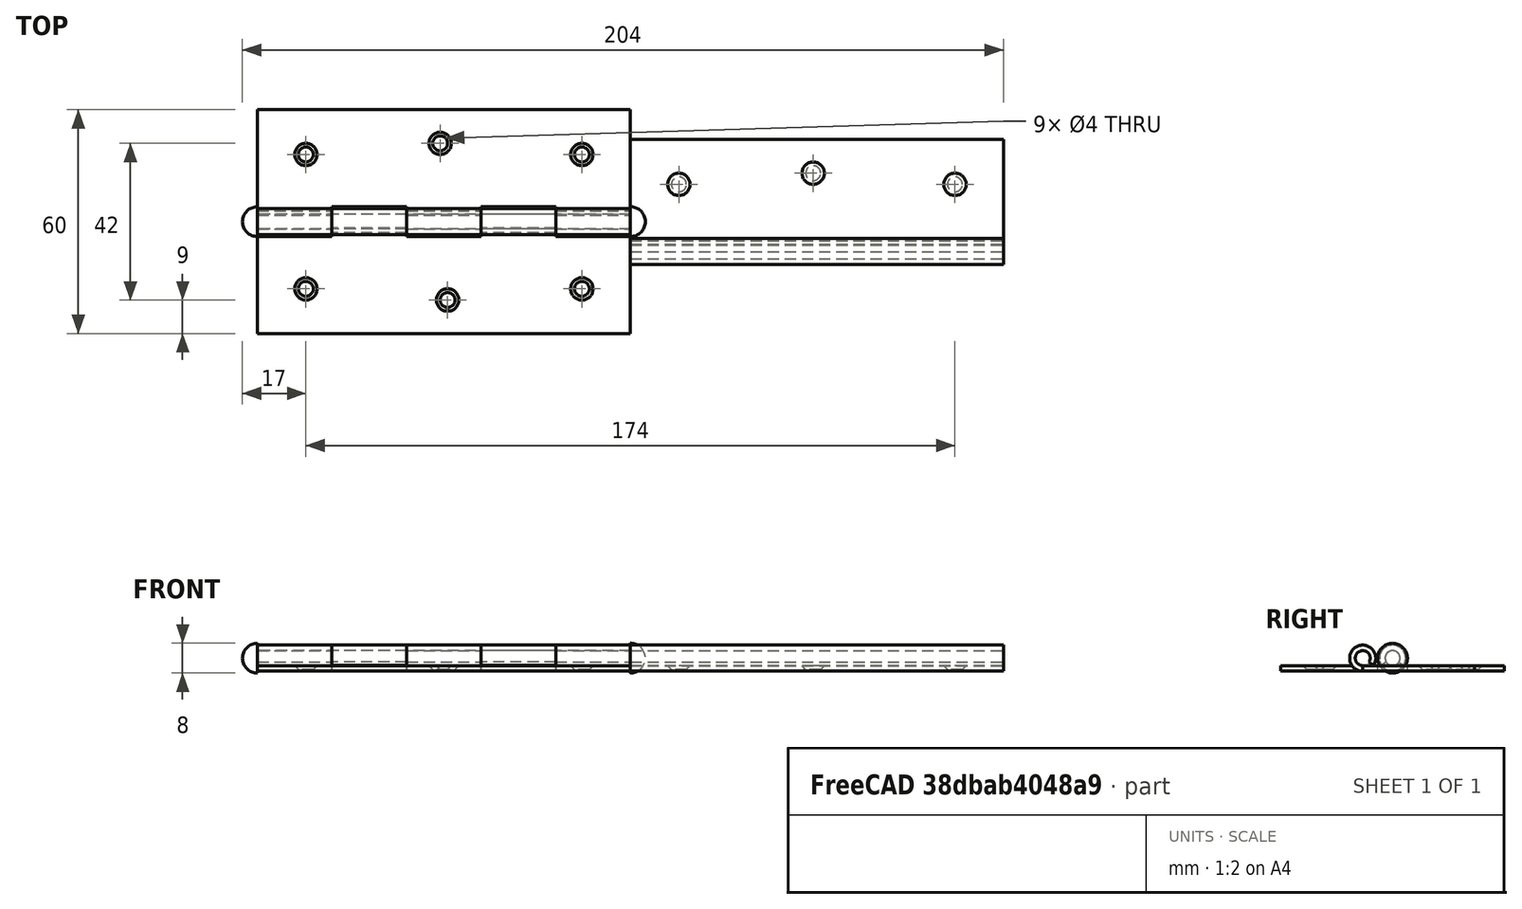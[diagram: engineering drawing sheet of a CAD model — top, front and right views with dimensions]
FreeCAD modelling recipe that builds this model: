
FCSTD DOCUMENT  (FreeCAD 0.18R13524 (Git))
Label: ABRAÇADEIRA
License: All rights reserved
LicenseURL: http://en.wikipedia.org/wiki/All_rights_reserved
objects: Part::Cut×11, Part::Box×7, Part::Cylinder×7, App::FeaturePython×3, Part::FeaturePython×2, Part::Chamfer×2, Part::Sphere×2, Part::MultiFuse×2, Part::Feature×1
note: 34 computed .brp shape members not serialized (recipe doc carries the construction recipe); baked Part::Feature solids carry a one-line shape summary decoded from their .brp

FEATURE [Part::Box] Box  label="Cube"
  AttacherType = Attacher::AttachEngine3D
  Height = 1.5
  Length = 100
  Width = 30
FEATURE [Part::FeaturePython] Bend  # WARN: FeaturePython — macro-defined, semantics opaque (R4)
  angle = 303
  baseObject = -> Box [Face3]
  gap1 = 0
  gap2 = 0
  invert = false
  length = 0
  miterangle1 = 0
  miterangle2 = 0
  radius = 2
  reliefd = 1
  reliefw = 0.5
FEATURE [Part::Cylinder] Cylinder
  Angle = 360
  AttacherType = Attacher::AttachEngine3D
  Height = 10
  Placement = pos=(13,18,0) rot=(0,0,1;0rad)
  Radius = 2
FEATURE [Part::Cylinder] Cylinder001
  Angle = 360
  AttacherType = Attacher::AttachEngine3D
  Height = 10
  Placement = pos=(49,21,0) rot=(0,0,1;0rad)
  Radius = 2
FEATURE [Part::Cylinder] Cylinder002
  Angle = 360
  AttacherType = Attacher::AttachEngine3D
  Height = 10
  Placement = pos=(87,18,0) rot=(0,0,1;0rad)
  Radius = 2
FEATURE [Part::Cut] Cut
  Base = -> Bend
  Tool = -> Cylinder
FEATURE [Part::Cut] Cut001
  Base = -> Cut
  Tool = -> Cylinder001
FEATURE [Part::Cut] Cut002
  Base = -> Cut001
  Tool = -> Cylinder002
FEATURE [Part::Chamfer] Chamfer
  Base = -> Cut002
  Edges = 3 edges r=1: [Edge11,Edge12,Edge13]
FEATURE [Part::Cylinder] Cylinder003
  Angle = 360
  AttacherType = Attacher::AttachEngine3D
  Height = 10
  Placement = pos=(13,18,0) rot=(0,0,1;0rad)
  Radius = 2
FEATURE [Part::Box] Box001  label="Cube001"
  AttacherType = Attacher::AttachEngine3D
  Height = 1.5
  Length = 100
  Width = 30
FEATURE [Part::Cylinder] Cylinder004
  Angle = 360
  AttacherType = Attacher::AttachEngine3D
  Height = 10
  Placement = pos=(49,21,0) rot=(0,0,1;0rad)
  Radius = 2
FEATURE [Part::Cylinder] Cylinder005
  Angle = 360
  AttacherType = Attacher::AttachEngine3D
  Height = 10
  Placement = pos=(87,18,0) rot=(0,0,1;0rad)
  Radius = 2
FEATURE [Part::FeaturePython] Bend001  # WARN: FeaturePython — macro-defined, semantics opaque (R4)
  angle = 303
  baseObject = -> Box001 [Face3]
  gap1 = 0
  gap2 = 0
  invert = false
  length = 0
  miterangle1 = 0
  miterangle2 = 0
  radius = 2
  reliefd = 1
  reliefw = 0.5
FEATURE [Part::Cut] Cut005
  Base = -> Bend001
  Tool = -> Cylinder003
FEATURE [Part::Cut] Cut004
  Base = -> Cut005
  Tool = -> Cylinder004
FEATURE [Part::Cut] Cut003
  Base = -> Cut004
  Tool = -> Cylinder005
FEATURE [Part::Chamfer] Chamfer001
  Base = -> Cut003
  Edges = 3 edges r=1: [Edge11,Edge12,Edge13]
FEATURE [Part::Feature] Chamfer002
  Placement = pos=(0,53,0) rot=(0,0,1;0rad)
  shape: bbox 100 x 33.5 x 7 mm, 14 faces (baked)
FEATURE [Part::Box] Box002  label="Cube002"
  AttacherType = Attacher::AttachEngine3D
  Height = 10
  Length = 20
  Placement = pos=(0,47,0) rot=(0,0,1;0rad)
  Width = 10
FEATURE [Part::Box] Box003  label="Cube003"
  AttacherType = Attacher::AttachEngine3D
  Height = 10
  Length = 20
  Placement = pos=(20,-6,0) rot=(0,0,1;0rad)
  Width = 10
FEATURE [Part::Box] Box004  label="Cube004"
  AttacherType = Attacher::AttachEngine3D
  Height = 10
  Length = 20
  Placement = pos=(40,47,0) rot=(0,0,1;0rad)
  Width = 10
FEATURE [Part::Box] Box005  label="Cube005"
  AttacherType = Attacher::AttachEngine3D
  Height = 10
  Length = 20
  Placement = pos=(60,-6,0) rot=(0,0,1;0rad)
  Width = 10
FEATURE [Part::Box] Box006  label="Cube006"
  AttacherType = Attacher::AttachEngine3D
  Height = 10
  Length = 20
  Placement = pos=(80,47,0) rot=(0,0,1;0rad)
  Width = 10
FEATURE [Part::Cut] Cut006
  Base = -> Chamfer001
  Tool = -> Box003
FEATURE [Part::Cut] Cut007
  Base = -> Cut006
  Placement = pos=(-100,8,0) rot=(0,0,1;0rad)
  Tool = -> Box005
FEATURE [Part::Cut] Cut008
  Base = -> Chamfer002
  Tool = -> Box002
FEATURE [Part::Cut] Cut009
  Base = -> Cut008
  Tool = -> Box004
FEATURE [Part::Cut] Cut010
  Base = -> Cut009
  Placement = pos=(0,61,0) rot=(0,0,-1;3.14159rad)
  Tool = -> Box006
FEATURE [App::FeaturePython] circularEdgeConstraint01  # a2plus constraint (typed FeaturePython)
  Object1 = Cut010
  Object2 = Cut007
  SubElement1 = Edge43
  SubElement2 = Edge22
  Type = circularEdge
  directionConstraint = 1
  lockRotation = false
  offset = 0
FEATURE [Part::Cylinder] Cylinder006
  Angle = 360
  AttacherType = Attacher::AttachEngine3D
  Height = 100
  Radius = 2
FEATURE [Part::Sphere] Sphere
  Angle1 = -90
  Angle2 = 90
  Angle3 = 180
  AttacherType = Attacher::AttachEngine3D
  Placement = pos=(0,0,0) rot=(1,0,0;4.71239rad)
  Radius = 4
FEATURE [Part::Sphere] Sphere001
  Angle1 = -90
  Angle2 = 90
  Angle3 = 180
  AttacherType = Attacher::AttachEngine3D
  Placement = pos=(0,0,100) rot=(1,0,0;1.5708rad)
  Radius = 4
FEATURE [Part::MultiFuse] Fusion
  Shapes = -> [Cylinder006,Sphere]
FEATURE [Part::MultiFuse] Fusion001
  Placement = pos=(0,8,3.5) rot=(0,-1,0;1.5708rad)
  Shapes = -> [Sphere001,Fusion]
FEATURE [App::FeaturePython] circularEdgeConstraint02  # a2plus constraint (typed FeaturePython)
  Object1 = Fusion001
  Object2 = Cut007
  SubElement1 = Edge16
  SubElement2 = Edge56
  Type = circularEdge
  directionConstraint = 0
  lockRotation = false
  offset = 0
FEATURE [App::FeaturePython] angleConstraint01  # a2plus constraint (typed FeaturePython)
  Object1 = Cut007
  Object2 = Cut010
  SubElement1 = Face1
  SubElement2 = Face1
  Type = angle_between_planes
  a = 360
  a_0_animatation = 180
  a_1_animatation = 360
  a_n_animatation = 42
  angle = 0
  animation_exp_animatation = a
  interp_method_animatation = none
  loop_animatation = true
  n_interp_animatation = 6
  play_after_generate_animatation = false
  timer_ms_animatation = 60
